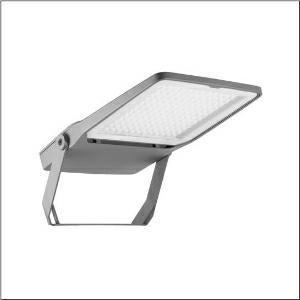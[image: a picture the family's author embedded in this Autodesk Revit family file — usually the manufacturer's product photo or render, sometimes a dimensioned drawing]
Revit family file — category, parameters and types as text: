
# Revit family: floodlight_fl_20_midi___pl43_5xa7681e2a1ac_2bcd
name_source: partatom
category: Lighting Fixtures
units: mm (PartAtom-declared; Revit-internal decimal feet)

## family parameters
Cut with Voids When Loaded = No
Host = Face
Light Source = No
Part Type = Normal
Room Calculation Point = No
Round Connector Dimension = Use Diameter
Shared = No

## types (1)
- Floodlight FL 20 midi  PL43 (1 x LED 4000K / CRI = 70 (unbekannt), 28460 lm, 4000K)
    Apparent Load = 208 VA
    CIE Flux Codes = 32 74 99 100 100
    Color Rendering = 70
    Color Temperature = 4000K
    Default Elevation = 1800 mm
    Description = Floodlight FL 20 midi, floodlight, primary light control with lens, of plastic, primary optical cover: protective disc, of toughened safety glass, transparent, light distribution: PL43, light emission: direct distribution, primary light characteristic: asymmetric, installation type: surface-mounted, LED High Power LED, rated luminous flux: 28.460 lm, light colour: 740, colour temperature: 4000K, control gear: ECG Basic, control: power reduction, overheat protection, electronic power reduction, with terminal, 5-pole, max. 2.5mm², mains connection: 220..240V, AC, 50/60Hz, rated input power: 208W, LED unit, of diecast aluminium, powder-coated, Siteco® metallic grey (DB 702S), length: 654 mm, width: 450 mm, height: 76mm, housing frame, of diecast aluminium, powder-coated, Siteco® metallic grey (DB 702S), mounting bracket, of steel, powder-coated, Siteco® metallic grey (DB 702S), ON/OFFprotection rating (complete): IP66, insulation class (complete): insulation class I (protective earthing), certification: CE, ENEC, VDE, protection symbol: D, permissible ambient temperature for indoor applications: -40..+40°C, permissible ambient temperature for outdoor applications: -40..+50°C, standard: DIN EN 12944, packaging unit: 1 piece

Light Distribution: PL43
    Height = 76 mm
    Lamp = 1 x LED 4000K / CRI >= 70 (unbekannt)
    Lamp Light Flux = 28460 lm
    Lamp count = 1
    Length = 672 mm
    Luminous efficacy = 137 lm/W
    Manufacturer = Siteco
    ModVariant = No
    Model = 5XA7681E2A1AC
    Number of Poles = 1
    OnlyDefault = Yes
    Power Factor = 1
    Product Name = Floodlight FL 20 midi | PL43
    Product group = floodlight | pylon top
    ProductGroupID = 6101
    Protection Class = Protection class I
    Protection Degree = IP 66
    RLX_Detail_Level = 1
    RlxData = <blob elided: 93921 chars, md5=287af720>
    Socket = socket
    Standby Power = 0 W
    System Light Flux = 28460 lm
    System Power = 208 W
    Type Comments = Product without accessories
    Type Image = l_1005943.jpg
    URL = http://relux.com
    VarID = ---
    Voltage = 0 V
    Weight = 0.00 kg
    Width = 450 mm

## geometry (parser evidence)
native form markers: Blend x4, Sweep x13
no freeform markers — native parametric forms only
